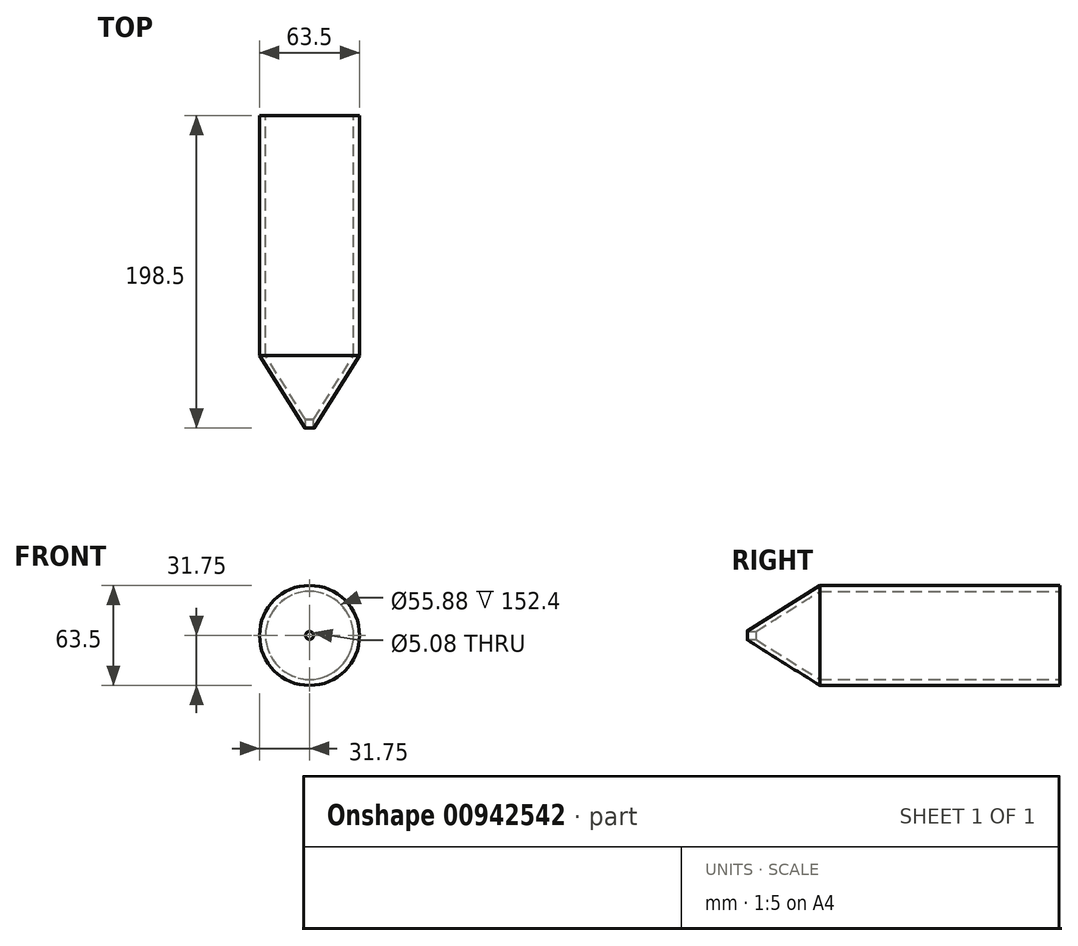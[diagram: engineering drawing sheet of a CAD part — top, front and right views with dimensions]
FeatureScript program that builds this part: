
annotation { "Feature Type Name" : "Feature", "Feature Type Description" : "" }
export const myFeature = defineFeature(function(context is Context, id is Id, definition is map)
    precondition{}
    {
        {
            var Q0;
            Q0=qCreatedBy(makeId("Front.planeOp"),FACE);
            var sketch = newSketch(context, id + "F0", { "sketchPlane" : qUnion([Q0])});
            skCircle(sketch, "E0", {"center": v(0, 0) * mm, "radius": 27.94 * mm});
            skCircle(sketch, "E1", {"center": v(0, 0) * mm, "radius": 31.75 * mm});
            skLineSegment(sketch, "E2", {"start": v(31.75, 0) * mm, "end": v(31.75, 51.41) * mm});
            skSolve(sketch);
        }
        {
            var Q0;
            Q0 = qSketchRegion(id + "F0", true);
            var Q1;
            Q1=makeQuery(id+"F0.imprint","IMPRINT",FACE,{"disambiguationData":[TD([[makeQuery(id+"F0.imprint","IMPRINT",EDGE,{"derivedFrom":sQuery(id+"F0.wireOp",EDGE,"E0")}),-1.0]])]});
            extrude(context, id + "F1", {"entities" : qUnion([Q0, Q1]), "endBound" : BoundingType.SYMMETRIC, "depth" : 152.4 * mm, "offsetDistance" : 25.4 * mm});
        }
        {
            var Q0;
            Q0=qCreatedBy(makeId("Top.planeOp"),FACE);
            var sketch = newSketch(context, id + "F2", { "sketchPlane" : qUnion([Q0])});
            skLineSegment(sketch, "E3", {"start": v(27.94, -76.2) * mm, "end": v(2.54, -116.84) * mm});
            skLineSegment(sketch, "E4", {"start": v(31.75, -76.2) * mm, "end": v(2.54, -122.94) * mm});
            skLineSegment(sketch, "E5", {"start": v(2.54, -122.94) * mm, "end": v(2.54, -116.84) * mm});
            skLineSegment(sketch, "E6", {"start": v(27.94, -76.2) * mm, "end": v(31.75, -76.2) * mm});
            skLineSegment(sketch, "E7", {"start": v(0, 0) * mm, "end": v(0, -129.5) * mm});
            skSolve(sketch);
        }
        {
            var Q0;
            Q0 = qSketchRegion(id + "F2", true);
            var Q1;
            Q1=sQuery(id+"F2.wireOp",EDGE,"E7");
            revolve(context, id + "F3", {"operationType" : NewBodyOperationType.ADD, "surfaceOperationType" : NewSurfaceOperationType.NEW, "entities" : qUnion([Q0]), "axis" : qUnion([Q1]), "revolveType" : RevolveType.FULL});
        }
        {
            var Q0;
            Q0=makeQuery(id+"F3.opRevolve","SWEPT_EDGE",EDGE,{"disambiguationData":[OSD([sQuery(id+"F2.wireOp",EDGE,"E4"),sQuery(id+"F2.wireOp",EDGE,"E5")])]});
            fillet(context, id + "F4", {"entities" : qUnion([Q0]), "radius" : 0.25 * mm, "tangentPropagation" : true, "allowEdgeOverflow" : false});
        }
    });
